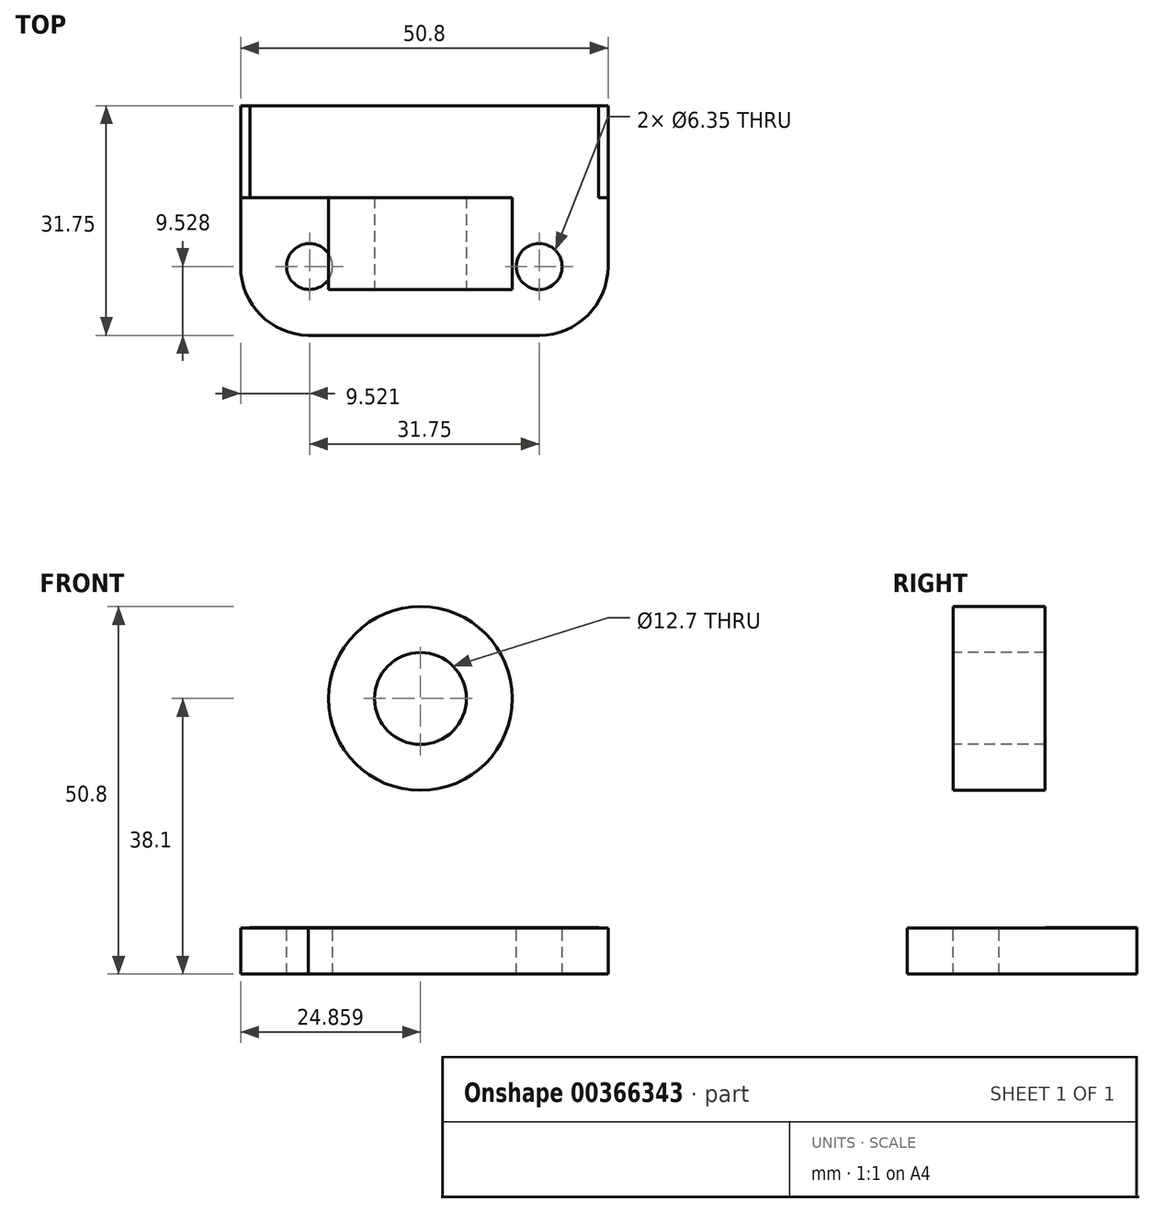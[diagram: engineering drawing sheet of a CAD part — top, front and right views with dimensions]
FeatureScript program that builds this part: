
annotation { "Feature Type Name" : "Feature", "Feature Type Description" : "" }
export const myFeature = defineFeature(function(context is Context, id is Id, definition is map)
    precondition{}
    {
        {
            var Q0;
            Q0=qCreatedBy(makeId("Top.planeOp"),FACE);
            var sketch = newSketch(context, id + "F0", { "sketchPlane" : qUnion([Q0])});
            skLineSegment(sketch, "E0", {"start": v(-9.38, 25.22) * mm, "end": v(41.42, 25.22) * mm});
            skLineSegment(sketch, "E1", {"start": v(41.42, 25.22) * mm, "end": v(41.42, -6.53) * mm});
            skLineSegment(sketch, "E2", {"start": v(41.42, -6.53) * mm, "end": v(-9.38, -6.53) * mm});
            skLineSegment(sketch, "E3", {"start": v(-9.38, -6.53) * mm, "end": v(-9.38, 25.22) * mm});
            skSolve(sketch);
        }
        {
            var Q0;
            Q0 = qSketchRegion(id + "F0", true);
            extrude(context, id + "F1", {"entities" : qUnion([Q0]), "depth" : 6.35 * mm});
        }
        {
            var Q0;
            Q0=makeQuery(id+"F1.opExtrude","CAP_FACE",FACE,{"disambiguationData":[OSD([sQuery(id+"F0.wireOp",EDGE,"E0"),sQuery(id+"F0.wireOp",EDGE,"E1"),sQuery(id+"F0.wireOp",EDGE,"E2"),sQuery(id+"F0.wireOp",EDGE,"E3")])],"isStart":false});
            var sketch = newSketch(context, id + "F2", { "sketchPlane" : qUnion([Q0])});
            skLineSegment(sketch, "E4", {"start": v(-9.38, 12.52) * mm, "end": v(41.42, 12.52) * mm});
            skSolve(sketch);
        }
        {
            var Q0;
            Q0 = qSketchRegion(id + "F2", true);
            var Q1;
            {var subQ0=sQuery(id+"F2.wireOp",EDGE,"E4");Q1=makeQuery(id+"F2.imprint","IMPRINT",FACE,{"disambiguationData":[TD([[makeQuery(id+"F2.imprint","IMPRINT",EDGE,{"derivedFrom":subQ0}),1.0]])]});}
            extrude(context, id + "F3", {"entities" : qUnion([Q0, Q1]), "operationType" : NewBodyOperationType.ADD, "depth" : 7 / 101.6 * mm});
        }
        {
            var Q0;
            Q0=makeQuery(id+"F1.opExtrude","CAP_FACE",FACE,{"disambiguationData":[OSD([sQuery(id+"F0.wireOp",EDGE,"E0"),sQuery(id+"F0.wireOp",EDGE,"E1"),sQuery(id+"F0.wireOp",EDGE,"E2"),sQuery(id+"F0.wireOp",EDGE,"E3")])],"isStart":false});
            var sketch = newSketch(context, id + "F4", { "sketchPlane" : qUnion([Q0])});
            skCircle(sketch, "E5", {"center": v(0.14, 3) * mm, "radius": 3.18 * mm});
            skCircle(sketch, "E6", {"center": v(31.9, 3) * mm, "radius": 3.18 * mm});
            skArc(sketch, "E7", {"start": v(-9.38, 3) * mm, "mid": v(-6.64, -3.68) * mm, "end": v(0, -6.53) * mm});
            skArc(sketch, "E8", {"start": v(31.9, -6.53) * mm, "mid": v(38.62, -3.73) * mm, "end": v(41.42, 3) * mm});
            skSolve(sketch);
        }
        {
            var Q0;
            Q0 = qSketchRegion(id + "F4", true);
            var Q1;
            {var subQ0=sQuery(id+"F4.wireOp",EDGE,"E8");Q1=makeQuery(id+"F4.imprint","IMPRINT",FACE,{"disambiguationData":[TD([[makeQuery(id+"F4.imprint","IMPRINT",EDGE,{"derivedFrom":subQ0}),-1.0]])]});}
            var Q2;
            {var subQ0=sQuery(id+"F4.wireOp",EDGE,"E7");Q2=makeQuery(id+"F4.imprint","IMPRINT",FACE,{"disambiguationData":[TD([[makeQuery(id+"F4.imprint","IMPRINT",EDGE,{"derivedFrom":subQ0}),-1.0]])]});}
            extrude(context, id + "F5", {"entities" : qUnion([Q0, Q1, Q2]), "operationType" : NewBodyOperationType.REMOVE, "oppositeDirection" : true, "depth" : 6.35 * mm});
        }
        {
            var Q0;
            Q0=makeQuery(id+"F3.opExtrude","SWEPT_FACE",FACE,{"disambiguationData":[OSD([sQuery(id+"F2.wireOp",EDGE,"E4")])]});
            var sketch = newSketch(context, id + "F6", { "sketchPlane" : qUnion([Q0])});
            skLineSegment(sketch, "E9", {"start": v(-9.38, 19.05) * mm, "end": v(41.42, 19.05) * mm});
            skLineSegment(sketch, "E10", {"start": v(3.32, 19.05) * mm, "end": v(3.32, 6.35) * mm});
            skLineSegment(sketch, "E11", {"start": v(28.72, 19.05) * mm, "end": v(28.72, 6.35) * mm});
            skArc(sketch, "E12", {"start": v(-9.38, 6.35) * mm, "mid": v(-0.4, 10.07) * mm, "end": v(3.32, 19.05) * mm});
            skArc(sketch, "E13", {"start": v(28.72, 19.05) * mm, "mid": v(32.44, 10.07) * mm, "end": v(41.42, 6.35) * mm});
            skCircle(sketch, "E14", {"center": v(15.48, 38.1) * mm, "radius": 12.7 * mm});
            skCircle(sketch, "E15", {"center": v(15.48, 38.1) * mm, "radius": 6.35 * mm});
            skLineSegment(sketch, "E16", {"start": v(3.32, 19.05) * mm, "end": v(2.78, 37.74) * mm});
            skLineSegment(sketch, "E17", {"start": v(28.72, 19.05) * mm, "end": v(28.17, 38.45) * mm});
            skSolve(sketch);
        }
        {
            var Q0;
            Q0=makeQuery(id+"F6.imprint","IMPRINT",FACE,{"disambiguationData":[TD([[makeQuery(id+"F6.imprint","IMPRINT",EDGE,{"derivedFrom":sQuery(id+"F6.wireOp",EDGE,"E15")}),1.0]])]});
            var Q1;
            {var subQ0=sQuery(id+"F6.wireOp",EDGE,"E16");Q1=makeQuery(id+"F6.imprint","IMPRINT",FACE,{"disambiguationData":[TD([[makeQuery(id+"F6.imprint","IMPRINT",EDGE,{"derivedFrom":subQ0}),1.0]])]});}
            var Q2;
            {var subQ6=sQuery(id+"F6.wireOp",EDGE,"E17");Q2=makeQuery(id+"F6.imprint","IMPRINT",FACE,{"disambiguationData":[TD([[makeQuery(id+"F6.imprint","IMPRINT",EDGE,{"derivedFrom":subQ6}),-1.0]])]});}
            var Q3;
            {var subQ4=sQuery(id+"F6.wireOp",EDGE,"E12");Q3=makeQuery(id+"F6.imprint","IMPRINT",FACE,{"disambiguationData":[TD([[makeQuery(id+"F6.imprint","IMPRINT",EDGE,{"derivedFrom":subQ4}),1.0]])]});}
            var Q4;
            {var subQ4=sQuery(id+"F6.wireOp",EDGE,"E13");Q4=makeQuery(id+"F6.imprint","IMPRINT",FACE,{"disambiguationData":[TD([[makeQuery(id+"F6.imprint","IMPRINT",EDGE,{"derivedFrom":subQ4}),1.0]])]});}
            extrude(context, id + "F7", {"entities" : qUnion([Q0, Q1, Q2, Q3, Q4]), "operationType" : NewBodyOperationType.REMOVE, "oppositeDirection" : true, "depth" : 12.7 * mm});
        }
        {
            var Q0;
            Q0=makeQuery(id+"F3.opExtrude","SWEPT_FACE",FACE,{"disambiguationData":[OSD([sQuery(id+"F2.wireOp",EDGE,"E4")])]});
            var sketch = newSketch(context, id + "F8", { "sketchPlane" : qUnion([Q0])});
            skCircle(sketch, "E18", {"center": v(15.48, 38.1) * mm, "radius": 12.7 * mm});
            skSolve(sketch);
        }
        {
            var Q0;
            Q0 = qSketchRegion(id + "F8", true);
            extrude(context, id + "F9", {"entities" : qUnion([Q0]), "operationType" : NewBodyOperationType.ADD, "depth" : 12.7 * mm});
        }
        {
            var Q0;
            Q0=makeQuery(id+"F9.opExtrude","CAP_FACE",FACE,{"disambiguationData":[OSD([sQuery(id+"F8.wireOp",EDGE,"E18")])],"isStart":false});
            var sketch = newSketch(context, id + "F10", { "sketchPlane" : qUnion([Q0])});
            skCircle(sketch, "E19", {"center": v(15.48, 38.1) * mm, "radius": 6.35 * mm});
            skSolve(sketch);
        }
        {
            var Q0;
            Q0 = qSketchRegion(id + "F10", true);
            extrude(context, id + "F11", {"entities" : qUnion([Q0]), "operationType" : NewBodyOperationType.REMOVE, "oppositeDirection" : true, "depth" : 25.4 * mm});
        }
    });
